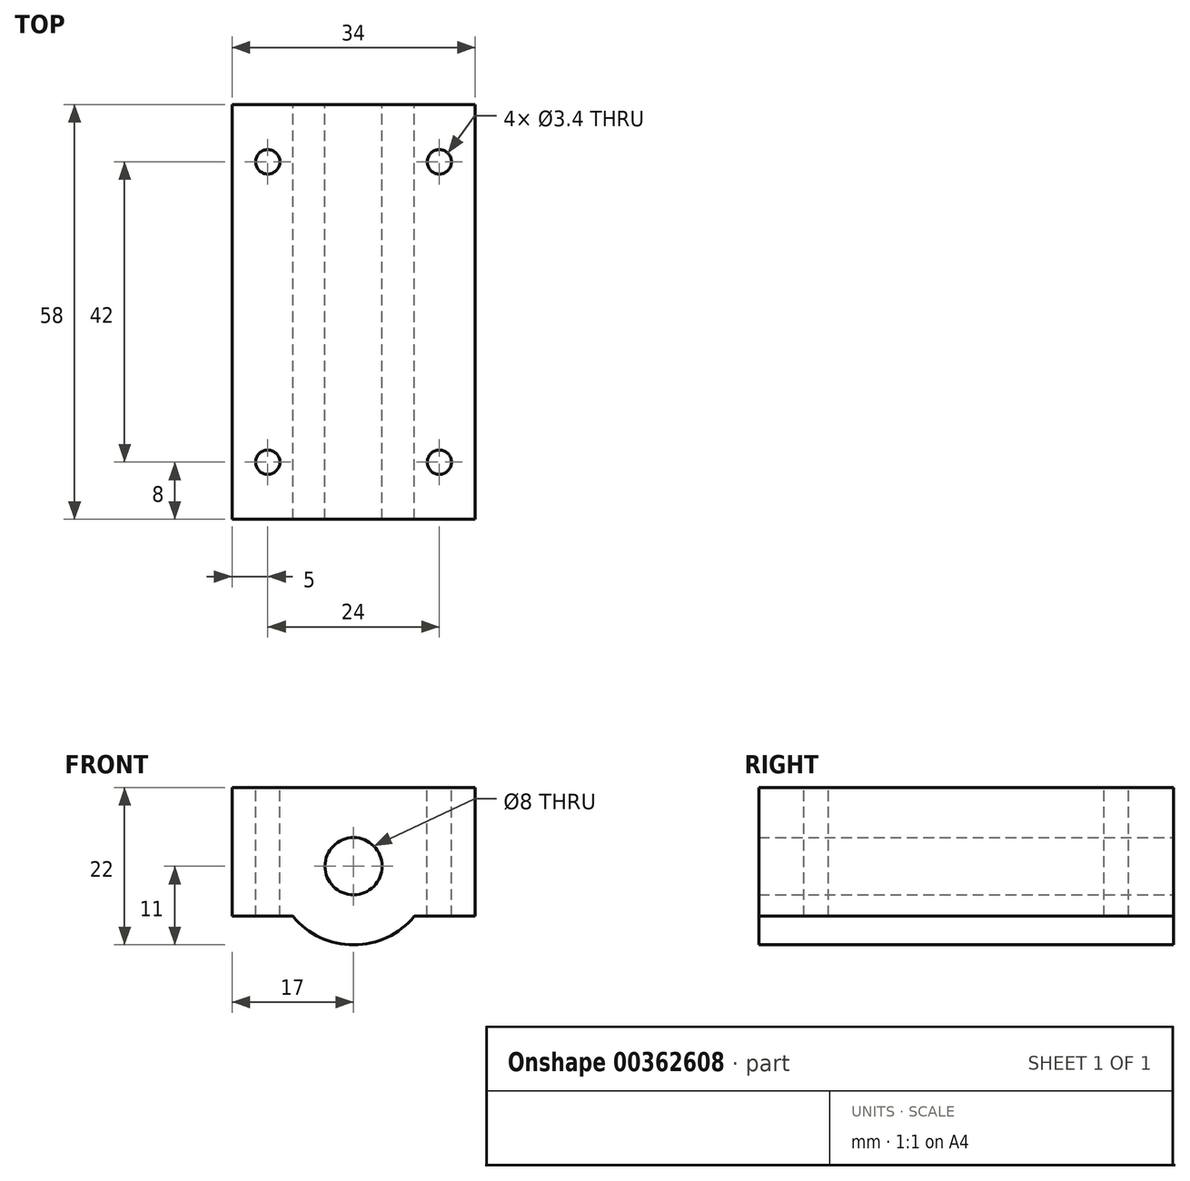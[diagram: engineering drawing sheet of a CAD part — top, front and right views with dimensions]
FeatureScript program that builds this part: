
annotation { "Feature Type Name" : "Feature", "Feature Type Description" : "" }
export const myFeature = defineFeature(function(context is Context, id is Id, definition is map)
    precondition{}
    {
        {
            var Q0;
            Q0=qCreatedBy(makeId("Front.planeOp"),FACE);
            var sketch = newSketch(context, id + "F0", { "sketchPlane" : qUnion([Q0])});
            skPoint(sketch, "E0.middle", {"position": v(0, 0) * mm});
            skArc(sketch, "E1", {"start": v(-8.49, -7) * mm, "mid": v(0, -11) * mm, "end": v(8.49, -7) * mm});
            skLineSegment(sketch, "E2.0", {"start": v(-17, 11) * mm, "end": v(17, 11) * mm});
            skLineSegment(sketch, "E3.0", {"start": v(-17, -7) * mm, "end": v(-8.49, -7) * mm});
            skLineSegment(sketch, "E4.0", {"start": v(17, -7) * mm, "end": v(17, 11) * mm});
            skLineSegment(sketch, "E5.0", {"start": v(-17, -7) * mm, "end": v(-17, 11) * mm});
            skLineSegment(sketch, "E6.trimOffspring", {"start": v(8.49, -7) * mm, "end": v(17, -7) * mm});
            skCircle(sketch, "E7", {"center": v(0, 0) * mm, "radius": 4 * mm});
            skSolve(sketch);
        }
        {
            var Q0;
            Q0 = qSketchRegion(id + "F0", true);
            var Q1;
            Q1 = qSketchRegion(id + "F2", true);
            extrude(context, id + "F1", {"entities" : qUnion([Q0, Q1]), "depth" : 58 * mm});
        }
        {
            var Q0;
            Q0=qCreatedBy(makeId("Top.planeOp"),FACE);
            var sketch = newSketch(context, id + "F2", { "sketchPlane" : qUnion([Q0])});
            skPoint(sketch, "E8", {"position": v(-12, -8) * mm});
            skPoint(sketch, "E9", {"position": v(12, -8) * mm});
            skPoint(sketch, "E10", {"position": v(12, -50) * mm});
            skPoint(sketch, "E11", {"position": v(-12, -50) * mm});
            skCircle(sketch, "E12", {"center": v(-12, -8) * mm, "radius": 1.7 * mm});
            skCircle(sketch, "E13", {"center": v(12, -8) * mm, "radius": 1.7 * mm});
            skCircle(sketch, "E14", {"center": v(12, -50) * mm, "radius": 1.7 * mm});
            skCircle(sketch, "E15", {"center": v(-12, -50) * mm, "radius": 1.7 * mm});
            skSolve(sketch);
        }
        {
            var Q0;
            Q0 = qSketchRegion(id + "F2", true);
            extrude(context, id + "F3", {"entities" : qUnion([Q0]), "operationType" : NewBodyOperationType.REMOVE, "endBound" : BoundingType.THROUGH_ALL, "oppositeDirection" : true, "depth" : 25 * mm});
        }
        {
            var Q0;
            Q0 = qSketchRegion(id + "F2", true);
            extrude(context, id + "F4", {"entities" : qUnion([Q0]), "operationType" : NewBodyOperationType.REMOVE, "endBound" : BoundingType.THROUGH_ALL, "oppositeDirection" : true, "depth" : 25 * mm});
        }
        {
            var Q0;
            Q0 = qSketchRegion(id + "F2", true);
            extrude(context, id + "F5", {"entities" : qUnion([Q0]), "operationType" : NewBodyOperationType.REMOVE, "oppositeDirection" : true, "depth" : -50 * mm});
        }
    });
